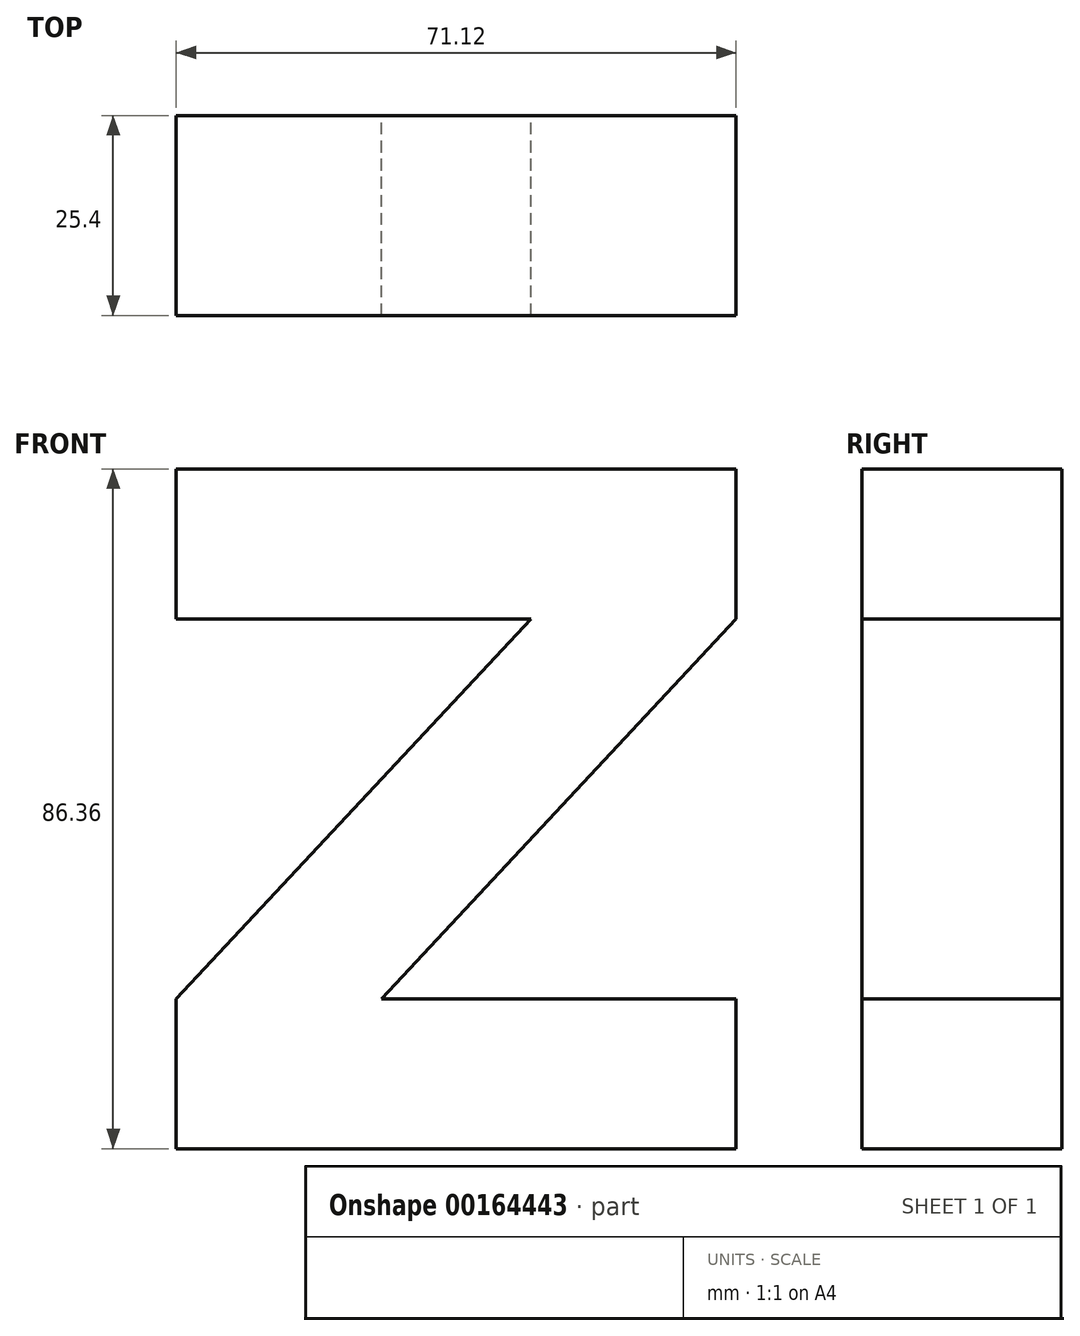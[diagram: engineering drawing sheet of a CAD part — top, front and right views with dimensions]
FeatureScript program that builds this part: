
annotation { "Feature Type Name" : "Feature", "Feature Type Description" : "" }
export const myFeature = defineFeature(function(context is Context, id is Id, definition is map)
    precondition{}
    {
        {
            var Q0;
            Q0=qCreatedBy(makeId("Front.planeOp"),FACE);
            var sketch = newSketch(context, id + "F0", { "sketchPlane" : qUnion([Q0])});
            skLineSegment(sketch, "E0", {"start": v(-32.66, 49.84) * mm, "end": v(38.46, 49.84) * mm});
            skLineSegment(sketch, "E1", {"start": v(-32.66, -36.52) * mm, "end": v(38.46, -36.52) * mm});
            skLineSegment(sketch, "E2", {"start": v(-32.66, 49.84) * mm, "end": v(-32.66, 30.79) * mm, "construction": true});
            skLineSegment(sketch, "E3", {"start": v(38.46, 49.84) * mm, "end": v(38.46, 30.79) * mm, "construction": true});
            skLineSegment(sketch, "E4", {"start": v(-32.66, 49.84) * mm, "end": v(-32.66, 30.79) * mm});
            skLineSegment(sketch, "E5", {"start": v(12.4, 30.79) * mm, "end": v(-32.66, -17.47) * mm});
            skLineSegment(sketch, "E6", {"start": v(12.4, 30.79) * mm, "end": v(-32.66, 30.79) * mm});
            skLineSegment(sketch, "E7", {"start": v(-32.66, -17.47) * mm, "end": v(-32.66, -36.52) * mm});
            skLineSegment(sketch, "E8", {"start": v(38.46, -36.52) * mm, "end": v(38.46, -17.47) * mm});
            skLineSegment(sketch, "E9", {"start": v(38.46, -17.47) * mm, "end": v(-6.6, -17.47) * mm});
            skLineSegment(sketch, "E10", {"start": v(-6.6, -17.47) * mm, "end": v(38.46, 30.79) * mm});
            skLineSegment(sketch, "E11", {"start": v(38.46, 30.79) * mm, "end": v(38.46, 49.84) * mm});
            skLineSegment(sketch, "E12.trimOffspring", {"start": v(-32.66, -17.47) * mm, "end": v(-32.66, -36.52) * mm, "construction": true});
            skLineSegment(sketch, "E13.trimOffspring", {"start": v(38.46, -17.47) * mm, "end": v(38.46, -36.52) * mm, "construction": true});
            skSolve(sketch);
        }
        {
            var Q0;
            Q0=makeQuery(id+"F0.imprint","IMPRINT",FACE,{"disambiguationData":[TD([[makeQuery(id+"F0.imprint","IMPRINT",EDGE,{"derivedFrom":sQuery(id+"F0.wireOp",EDGE,"E0")}),-1.0]])]});
            extrude(context, id + "F1", {"entities" : qUnion([Q0]), "depth" : 25.4 * mm});
        }
    });
